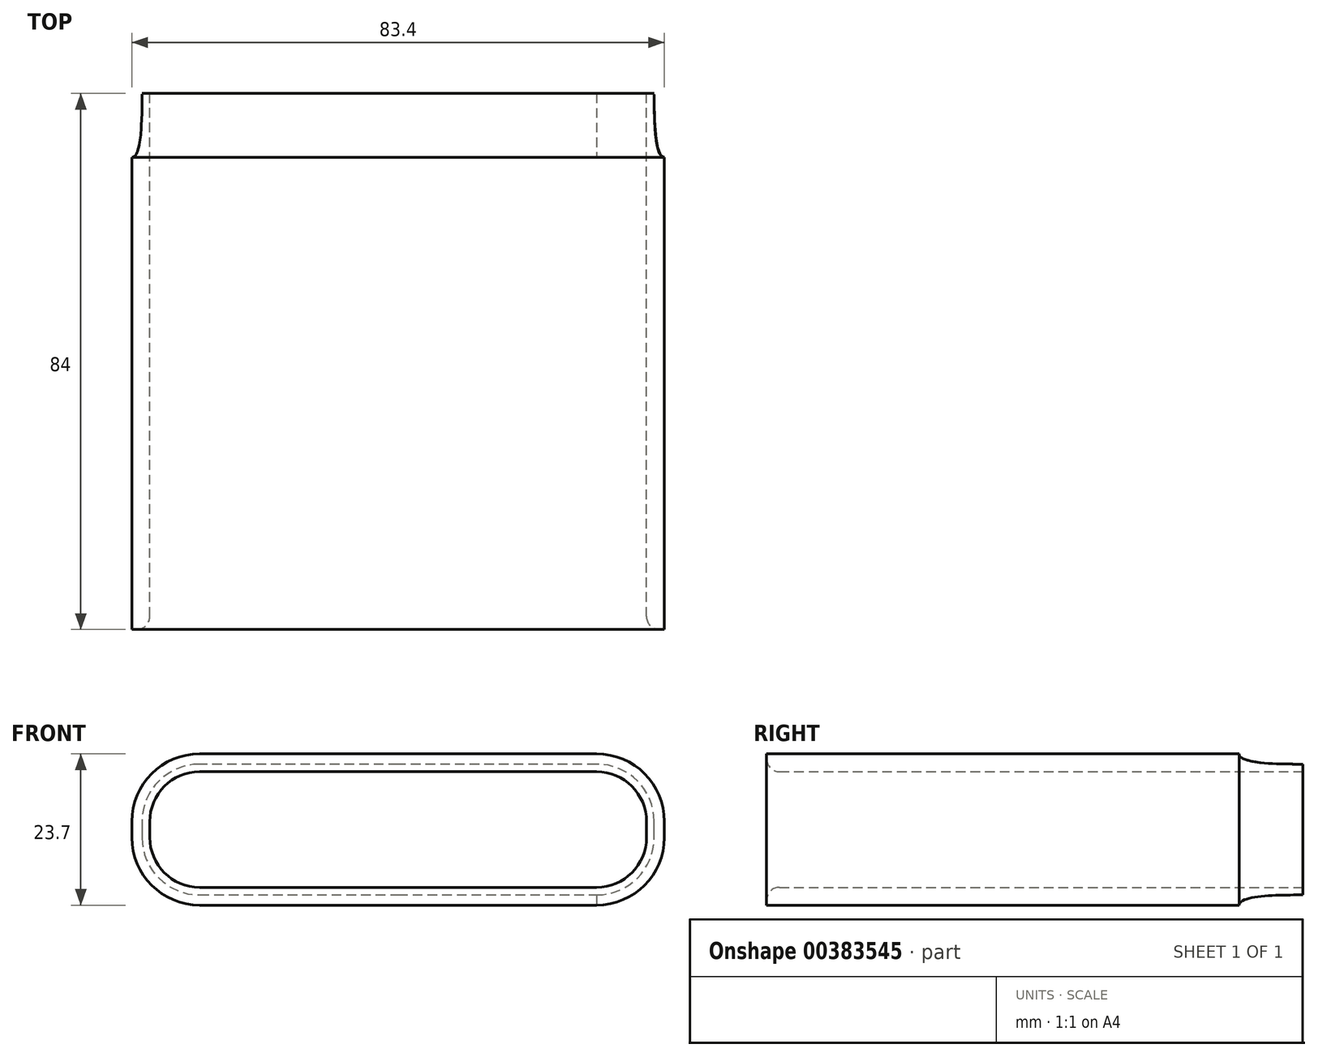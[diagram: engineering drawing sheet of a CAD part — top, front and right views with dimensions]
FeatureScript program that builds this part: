
annotation { "Feature Type Name" : "Feature", "Feature Type Description" : "" }
export const myFeature = defineFeature(function(context is Context, id is Id, definition is map)
    precondition{}
    {
        {
            var Q0;
            Q0=qCreatedBy(makeId("Front.planeOp"),FACE);
            var sketch = newSketch(context, id + "F0", { "sketchPlane" : qUnion([Q0])});
            skArc(sketch, "E0", {"start": v(-31.1, 11.85) * mm, "mid": v(-38.6, 8.75) * mm, "end": v(-41.7, 1.25) * mm});
            skLineSegment(sketch, "E1", {"start": v(-31.1, 11.85) * mm, "end": v(0, 11.85) * mm});
            skLineSegment(sketch, "E2", {"start": v(-41.7, 1.25) * mm, "end": v(-41.7, 0) * mm});
            skLineSegment(sketch, "E3.MirrorCS", {"start": v(41.7, 1.25) * mm, "end": v(41.7, 0) * mm});
            skArc(sketch, "E4.MirrorCS", {"start": v(31.1, 11.85) * mm, "mid": v(38.6, 8.75) * mm, "end": v(41.7, 1.25) * mm});
            skLineSegment(sketch, "E5.MirrorCS", {"start": v(31.1, 11.85) * mm, "end": v(0, 11.85) * mm});
            skLineSegment(sketch, "E6.MirrorCS", {"start": v(-41.7, -1.25) * mm, "end": v(-41.7, 0) * mm});
            skArc(sketch, "E7.MirrorCS", {"start": v(-31.1, -11.85) * mm, "mid": v(-38.6, -8.75) * mm, "end": v(-41.7, -1.25) * mm});
            skLineSegment(sketch, "E8.MirrorCS", {"start": v(-31.1, -11.85) * mm, "end": v(0, -11.85) * mm});
            skLineSegment(sketch, "E9.MirrorCS", {"start": v(31.1, -11.85) * mm, "end": v(0, -11.85) * mm});
            skArc(sketch, "E10.MirrorCS", {"start": v(31.1, -11.85) * mm, "mid": v(38.6, -8.75) * mm, "end": v(41.7, -1.25) * mm});
            skLineSegment(sketch, "E11.MirrorCS", {"start": v(41.7, -1.25) * mm, "end": v(41.7, 0) * mm});
            skArc(sketch, "E12", {"start": v(-31.1, 10.25) * mm, "mid": v(-37.46, 7.61) * mm, "end": v(-40.1, 1.25) * mm});
            skArc(sketch, "E13", {"start": v(-31.1, 9.05) * mm, "mid": v(-36.62, 6.77) * mm, "end": v(-38.9, 1.25) * mm});
            skLineSegment(sketch, "E14", {"start": v(-40.1, 1.25) * mm, "end": v(-40.1, 0) * mm});
            skLineSegment(sketch, "E15", {"start": v(-31.1, 10.25) * mm, "end": v(0, 10.25) * mm});
            skLineSegment(sketch, "E16", {"start": v(-38.9, 1.25) * mm, "end": v(-38.9, 0) * mm});
            skLineSegment(sketch, "E17", {"start": v(-31.1, 9.05) * mm, "end": v(0, 9.05) * mm});
            skLineSegment(sketch, "E18.MirrorCS", {"start": v(31.1, 9.05) * mm, "end": v(0, 9.05) * mm});
            skLineSegment(sketch, "E19.MirrorCS", {"start": v(31.1, 10.25) * mm, "end": v(0, 10.25) * mm});
            skArc(sketch, "E20.MirrorCS", {"start": v(31.1, 10.25) * mm, "mid": v(37.46, 7.61) * mm, "end": v(40.1, 1.25) * mm});
            skArc(sketch, "E21.MirrorCS", {"start": v(31.1, 9.05) * mm, "mid": v(36.62, 6.77) * mm, "end": v(38.9, 1.25) * mm});
            skLineSegment(sketch, "E22.MirrorCS", {"start": v(38.9, 1.25) * mm, "end": v(38.9, 0) * mm});
            skLineSegment(sketch, "E23.MirrorCS", {"start": v(40.1, 1.25) * mm, "end": v(40.1, 0) * mm});
            skLineSegment(sketch, "E24.MirrorCS", {"start": v(-40.1, -1.25) * mm, "end": v(-40.1, 0) * mm});
            skLineSegment(sketch, "E25.MirrorCS", {"start": v(-38.9, -1.25) * mm, "end": v(-38.9, 0) * mm});
            skArc(sketch, "E26.MirrorCS", {"start": v(-31.1, -10.25) * mm, "mid": v(-37.46, -7.61) * mm, "end": v(-40.1, -1.25) * mm});
            skLineSegment(sketch, "E27.MirrorCS", {"start": v(-31.1, -10.25) * mm, "end": v(0, -10.25) * mm});
            skLineSegment(sketch, "E28.MirrorCS", {"start": v(-31.1, -9.05) * mm, "end": v(0, -9.05) * mm});
            skLineSegment(sketch, "E29.MirrorCS", {"start": v(31.1, -9.05) * mm, "end": v(0, -9.05) * mm});
            skLineSegment(sketch, "E30.MirrorCS", {"start": v(31.1, -10.25) * mm, "end": v(0, -10.25) * mm});
            skArc(sketch, "E31.MirrorCS", {"start": v(31.1, -10.25) * mm, "mid": v(37.46, -7.61) * mm, "end": v(40.1, -1.25) * mm});
            skArc(sketch, "E32.MirrorCS", {"start": v(31.1, -9.05) * mm, "mid": v(36.62, -6.77) * mm, "end": v(38.9, -1.25) * mm});
            skLineSegment(sketch, "E33.MirrorCS", {"start": v(38.9, -1.25) * mm, "end": v(38.9, 0) * mm});
            skLineSegment(sketch, "E34.MirrorCS", {"start": v(40.1, -1.25) * mm, "end": v(40.1, 0) * mm});
            skArc(sketch, "E35.MirrorCS", {"start": v(-31.1, -9.05) * mm, "mid": v(-36.62, -6.77) * mm, "end": v(-38.9, -1.25) * mm});
            skSolve(sketch);
        }
        {
            var Q0;
            Q0=makeQuery(id+"F0.imprint","IMPRINT",FACE,{"disambiguationData":[TD([[makeQuery(id+"F0.imprint","IMPRINT",EDGE,{"derivedFrom":sQuery(id+"F0.wireOp",EDGE,"E0")}),1.0]])]});
            var Q1;
            Q1=makeQuery(id+"F0.imprint","IMPRINT",FACE,{"disambiguationData":[TD([[makeQuery(id+"F0.imprint","IMPRINT",EDGE,{"derivedFrom":sQuery(id+"F0.wireOp",EDGE,"E12")}),1.0]])]});
            extrude(context, id + "F1", {"entities" : qUnion([Q0, Q1]), "depth" : 74 * mm});
        }
        {
            var Q0;
            Q0=makeQuery(id+"F1.opExtrude","CAP_EDGE",EDGE,{"disambiguationData":[OSD([sQuery(id+"F0.wireOp",EDGE,"E16"),sQuery(id+"F0.wireOp",EDGE,"E25.MirrorCS")])],"isStart":false});
            var Q1;
            Q1=makeQuery(id+"F1.opExtrude","CAP_EDGE",EDGE,{"disambiguationData":[OSD([sQuery(id+"F0.wireOp",EDGE,"E17"),sQuery(id+"F0.wireOp",EDGE,"E18.MirrorCS")])],"isStart":false});
            var Q2;
            Q2=makeQuery(id+"F1.opExtrude","CAP_EDGE",EDGE,{"disambiguationData":[OSD([sQuery(id+"F0.wireOp",EDGE,"E13")])],"isStart":false});
            fillet(context, id + "F2", {"entities" : qUnion([Q0, Q1, Q2]), "radius" : 2.03 * mm, "tangentPropagation" : true, "allowEdgeOverflow" : false});
        }
        {
            var Q0;
            Q0=makeQuery(id+"F0.imprint","IMPRINT",FACE,{"disambiguationData":[TD([[makeQuery(id+"F0.imprint","IMPRINT",EDGE,{"derivedFrom":sQuery(id+"F0.wireOp",EDGE,"E13")}),1.0]])]});
            cPlane(context, id + "F3", {"entities" : qUnion([Q0]), "cplaneType" : CPlaneType.OFFSET, "offset" : 10 * mm, "oppositeDirection" : true, "width" : 150 * mm, "height" : 150 * mm});
        }
        {
            var Q0;
            Q0=qCreatedBy(id+"F3.planeOp",FACE);
            var sketch = newSketch(context, id + "F4", { "sketchPlane" : qUnion([Q0])});
            skArc(sketch, "E36.0.0", {"start": v(31.1, -10.25) * mm, "mid": v(37.46, -7.61) * mm, "end": v(40.1, -1.25) * mm});
            skLineSegment(sketch, "E36.0.1", {"start": v(40.1, -1.25) * mm, "end": v(40.1, 0) * mm});
            skLineSegment(sketch, "E36.0.2", {"start": v(40.1, 0) * mm, "end": v(40.1, 1.25) * mm});
            skArc(sketch, "E36.0.3", {"start": v(40.1, 1.25) * mm, "mid": v(37.46, 7.61) * mm, "end": v(31.1, 10.25) * mm});
            skLineSegment(sketch, "E36.0.4", {"start": v(31.1, 10.25) * mm, "end": v(0, 10.25) * mm});
            skLineSegment(sketch, "E36.0.5", {"start": v(0, 10.25) * mm, "end": v(-31.1, 10.25) * mm});
            skArc(sketch, "E36.0.6", {"start": v(-31.1, 10.25) * mm, "mid": v(-37.46, 7.61) * mm, "end": v(-40.1, 1.25) * mm});
            skLineSegment(sketch, "E36.0.7", {"start": v(-40.1, 1.25) * mm, "end": v(-40.1, 0) * mm});
            skLineSegment(sketch, "E36.0.8", {"start": v(-40.1, 0) * mm, "end": v(-40.1, -1.25) * mm});
            skArc(sketch, "E36.0.9", {"start": v(-40.1, -1.25) * mm, "mid": v(-37.46, -7.61) * mm, "end": v(-31.1, -10.25) * mm});
            skLineSegment(sketch, "E36.0.10", {"start": v(-31.1, -10.25) * mm, "end": v(0, -10.25) * mm});
            skLineSegment(sketch, "E36.0.11", {"start": v(0, -10.25) * mm, "end": v(31.1, -10.25) * mm});
            skSolve(sketch);
        }
        {
            var Q0;
            Q0=qCreatedBy(makeId("Front.planeOp"),FACE);
            var sketch = newSketch(context, id + "F5", { "sketchPlane" : qUnion([Q0])});
            skLineSegment(sketch, "E37.0", {"start": v(31.1, 11.85) * mm, "end": v(0, 11.85) * mm});
            skArc(sketch, "E38.0", {"start": v(31.1, 11.85) * mm, "mid": v(38.6, 8.75) * mm, "end": v(41.7, 1.25) * mm});
            skLineSegment(sketch, "E39.0", {"start": v(41.7, -1.25) * mm, "end": v(41.7, 0) * mm});
            skLineSegment(sketch, "E40.0", {"start": v(41.7, 1.25) * mm, "end": v(41.7, 0) * mm});
            skArc(sketch, "E41.0", {"start": v(31.1, -11.85) * mm, "mid": v(38.6, -8.75) * mm, "end": v(41.7, -1.25) * mm});
            skLineSegment(sketch, "E42.0", {"start": v(31.1, -11.85) * mm, "end": v(0, -11.85) * mm});
            skLineSegment(sketch, "E43.0", {"start": v(-31.1, 11.85) * mm, "end": v(0, 11.85) * mm});
            skArc(sketch, "E44.0", {"start": v(-31.1, 11.85) * mm, "mid": v(-38.6, 8.75) * mm, "end": v(-41.7, 1.25) * mm});
            skLineSegment(sketch, "E45.0", {"start": v(-41.7, 1.25) * mm, "end": v(-41.7, 0) * mm});
            skLineSegment(sketch, "E46.0", {"start": v(-41.7, -1.25) * mm, "end": v(-41.7, 0) * mm});
            skArc(sketch, "E47.0", {"start": v(-31.1, -11.85) * mm, "mid": v(-38.6, -8.75) * mm, "end": v(-41.7, -1.25) * mm});
            skLineSegment(sketch, "E48.0", {"start": v(-31.1, -11.85) * mm, "end": v(0, -11.85) * mm});
            skSolve(sketch);
        }
        {
            var Q1;
            Q1 = qSketchRegion(id + "F4", true);
            var Q2;
            Q2 = qSketchRegion(id + "F5", true);
            loft(context, id + "F6", {"operationType" : NewBodyOperationType.ADD, "startCondition" : LoftEndDerivativeType.NORMAL_TO_PROFILE, "startMagnitude" : 1, "endCondition" : LoftEndDerivativeType.TANGENT_TO_PROFILE, "endMagnitude" : 3, "sheetProfilesArray" : [{ "sheetProfileEntities" : qUnion([Q1]) }, { "sheetProfileEntities" : qUnion([Q2]) }]});
        }
        {
            var Q0;
            Q0=qCreatedBy(id+"F3.planeOp",FACE);
            var sketch = newSketch(context, id + "F7", { "sketchPlane" : qUnion([Q0])});
            skLineSegment(sketch, "E49.0", {"start": v(31.1, 9.05) * mm, "end": v(0, 9.05) * mm});
            skArc(sketch, "E50.0", {"start": v(31.1, 9.05) * mm, "mid": v(36.62, 6.77) * mm, "end": v(38.9, 1.25) * mm});
            skLineSegment(sketch, "E51.0", {"start": v(38.9, 1.25) * mm, "end": v(38.9, 0) * mm});
            skLineSegment(sketch, "E52.0", {"start": v(38.9, -1.25) * mm, "end": v(38.9, 0) * mm});
            skArc(sketch, "E53.0", {"start": v(31.1, -9.05) * mm, "mid": v(36.62, -6.77) * mm, "end": v(38.9, -1.25) * mm});
            skLineSegment(sketch, "E54.0", {"start": v(31.1, -9.05) * mm, "end": v(0, -9.05) * mm});
            skLineSegment(sketch, "E55.0", {"start": v(-31.1, -9.05) * mm, "end": v(0, -9.05) * mm});
            skLineSegment(sketch, "E56.0", {"start": v(-31.1, 9.05) * mm, "end": v(0, 9.05) * mm});
            skArc(sketch, "E57.0", {"start": v(-31.1, -9.05) * mm, "mid": v(-36.62, -6.77) * mm, "end": v(-38.9, -1.25) * mm});
            skLineSegment(sketch, "E58.0", {"start": v(-38.9, -1.25) * mm, "end": v(-38.9, 0) * mm});
            skLineSegment(sketch, "E59.0", {"start": v(-38.9, 1.25) * mm, "end": v(-38.9, 0) * mm});
            skArc(sketch, "E60.0", {"start": v(-31.1, 9.05) * mm, "mid": v(-36.62, 6.77) * mm, "end": v(-38.9, 1.25) * mm});
            skSolve(sketch);
        }
        {
            var Q0;
            Q0=makeQuery(id+"F7.imprint","IMPRINT",FACE,{"disambiguationData":[TD([[makeQuery(id+"F7.imprint","IMPRINT",EDGE,{"derivedFrom":sQuery(id+"F7.wireOp",EDGE,"E49.0")}),1.0]])]});
            extrude(context, id + "F8", {"entities" : qUnion([Q0]), "operationType" : NewBodyOperationType.REMOVE, "depth" : 20 * mm});
        }
    });
